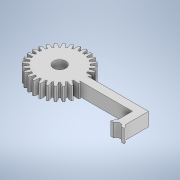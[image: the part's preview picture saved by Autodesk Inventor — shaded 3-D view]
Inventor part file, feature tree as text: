
AUTODESK INVENTOR PART (.ipt)
format: ipt  version: 2022 (Build 260153000, 153)  size: 300,544 bytes
history: native  units: in
note: dims shown in document units (in); Inventor stores cm internally (conversion verified against a paired STEP export)
features: extrude x5, sketch x5, pattern_circular x1
ambient origin geometry x8: Origin, YZ Plane, XZ Plane, XY Plane, X Axis, Y Axis, Z Axis, Center Point
bodies: Solid1 (feature_tree)
feature tree (11):
  extrude  "Extrusion1"  Depth=0.1575in
  pattern_circular  "Circular Pattern1"  [2 undecoded]
  extrude  "Extrusion6"  Depth=0.1969in
  extrude  "Extrusion7"  Depth=0.1969in TaperAngle=0.0deg
  extrude  "Extrusion8"  Depth=0.1969in TaperAngle=360.0deg
  extrude  "Extrusion9"  Depth=0.1969in
  sketch  "Sketch1"  dims[d0=0.6299in d1=0.1575in]
  sketch  "Sketch8"  dims[d2=0.0098in]
  sketch  "Sketch9"  dims[d3=0.0098in]
  sketch  "Sketch10"  dims[d4=0.0236in]
  sketch  "Sketch11"  dims[d7=0.0472in d8=0.1772in d10=0.0787in d11=0.1969in d12=0.0in d13=11.0236in d14=360.0deg d49=0.1969in d50=0.1575in d51=0.5438in d52=0.0in d53=1.1811in d54=0.7087in d55=0.748in d56=0.748in d57=0.1969in d58=0.9843in d59=0.0591in d60=0.0591in d61=0.0591in d62=0.3543in d63=0.0591in d64=0.1181in d65=0.1969in d66=0.0197in d67=0.0197in d68=0.0197in d69=0.1969in d70=0.0in d71=1.1811in d72=0.3543in d73=0.1181in d74=0.1181in d75=0.3543in d76=0.1181in d77=0.1969in d78=0.0197in d79=0.1969in d80=0.0197in d81=0.0197in d82=0.1969in d83=0.0in d84=0.1811in d85=0.1969in d86=0.0in]
note: 2 required parameter values undecoded (feature->parameter linkage not recoverable at this tier; creation-order binding heuristic only, values carry confidence <= 0.55)
